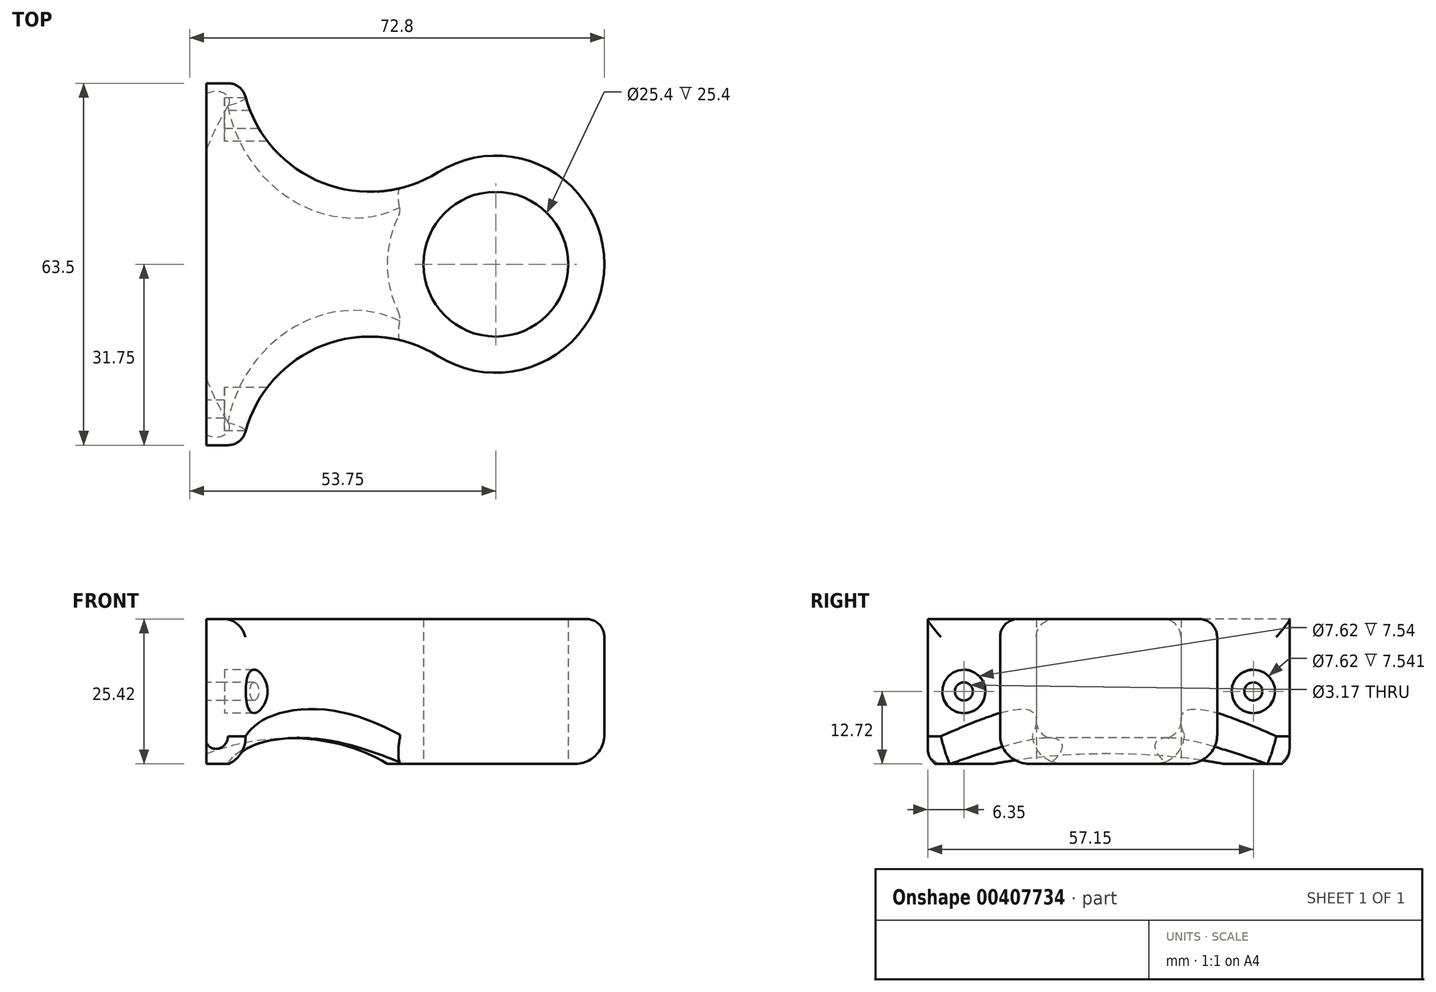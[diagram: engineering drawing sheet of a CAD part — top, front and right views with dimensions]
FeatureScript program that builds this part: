
annotation { "Feature Type Name" : "Feature", "Feature Type Description" : "" }
export const myFeature = defineFeature(function(context is Context, id is Id, definition is map)
    precondition{}
    {
        {
            var Q0;
            Q0=qCreatedBy(makeId("Top.planeOp"),FACE);
            var sketch = newSketch(context, id + "F0", { "sketchPlane" : qUnion([Q0])});
            skCircle(sketch, "E0", {"center": v(0, 0) * mm, "radius": 12.7 * mm});
            skCircle(sketch, "E1", {"center": v(0, 0) * mm, "radius": 19.05 * mm});
            skLineSegment(sketch, "E2", {"start": v(-44.45, 31.75) * mm, "end": v(-44.45, 0) * mm});
            skLineSegment(sketch, "E3", {"start": v(-50.8, 31.75) * mm, "end": v(-50.8, 0) * mm});
            skLineSegment(sketch, "E4", {"start": v(-50.8, 31.75) * mm, "end": v(-44.45, 31.75) * mm});
            skArc(sketch, "E5", {"start": v(-44.45, 31.75) * mm, "mid": v(-31.47, 14.73) * mm, "end": v(-10.1, 16.15) * mm});
            skArc(sketch, "E6.MirrorC", {"start": v(-44.45, -31.75) * mm, "mid": v(-31.47, -14.73) * mm, "end": v(-10.1, -16.15) * mm});
            skLineSegment(sketch, "E7.MirrorCS", {"start": v(-44.45, -31.75) * mm, "end": v(-44.45, 0) * mm});
            skLineSegment(sketch, "E8.MirrorCS", {"start": v(-50.8, -31.75) * mm, "end": v(-44.45, -31.75) * mm});
            skLineSegment(sketch, "E9.MirrorCS", {"start": v(-50.8, -31.75) * mm, "end": v(-50.8, 0) * mm});
            skSolve(sketch);
        }
        {
            var Q0;
            Q0=makeQuery(id+"F0.imprint","IMPRINT",FACE,{"disambiguationData":[TD([[makeQuery(id+"F0.imprint","IMPRINT",EDGE,{"derivedFrom":sQuery(id+"F0.wireOp",EDGE,"E2")}),1.0]])]});
            var Q1;
            Q1=makeQuery(id+"F0.imprint","IMPRINT",FACE,{"disambiguationData":[TD([[makeQuery(id+"F0.imprint","IMPRINT",EDGE,{"derivedFrom":sQuery(id+"F0.wireOp",EDGE,"E2")}),-1.0]])]});
            var Q2;
            Q2=makeQuery(id+"F0.imprint","IMPRINT",FACE,{"disambiguationData":[TD([[makeQuery(id+"F0.imprint","IMPRINT",EDGE,{"derivedFrom":sQuery(id+"F0.wireOp",EDGE,"E0")}),-1.0]])]});
            extrude(context, id + "F1", {"entities" : qUnion([Q0, Q1, Q2]), "depth" : 25.4 * mm, "offsetDistance" : 25.4 * mm});
        }
        {
            var Q0;
            Q0=makeQuery(id+"F1.opExtrude","CAP_VERTEX",VERTEX,{"disambiguationData":[OSD([sQuery(id+"F0.wireOp",EDGE,"E2"),sQuery(id+"F0.wireOp",EDGE,"E4"),sQuery(id+"F0.wireOp",EDGE,"E5")])],"isStart":true});
            var Q1;
            Q1=makeQuery(id+"F1.opExtrude","CAP_VERTEX",VERTEX,{"disambiguationData":[OSD([sQuery(id+"F0.wireOp",EDGE,"E1"),sQuery(id+"F0.wireOp",EDGE,"E5")])],"isStart":true});
            var Q2;
            Q2=makeQuery(id+"F1.opExtrude","CAP_VERTEX",VERTEX,{"disambiguationData":[OSD([sQuery(id+"F0.wireOp",EDGE,"E1"),sQuery(id+"F0.wireOp",EDGE,"E5")])],"isStart":false});
            cPlane(context, id + "F2", {"entities" : qUnion([Q0, Q1, Q2]), "cplaneType" : CPlaneType.THREE_POINT, "offset" : 25.4 * mm, "width" : 152.4 * mm, "height" : 152.4 * mm});
        }
        {
            var Q0;
            Q0=qCreatedBy(id+"F2.planeOp",FACE);
            var sketch = newSketch(context, id + "F3", { "sketchPlane" : qUnion([Q0])});
            skCircle(sketch, "E10", {"center": v(34.74, -37) * mm, "radius": 41.52 * mm});
            skLineSegment(sketch, "E11", {"start": v(8.8, 12.7) * mm, "end": v(68.21, 12.7) * mm});
            skCircle(sketch, "E12.MirrorC", {"center": v(34.74, 62.4) * mm, "radius": 41.52 * mm});
            skSolve(sketch);
        }
        {
            var Q0;
            Q0=makeQuery(id+"F3.imprint","IMPRINT",FACE,{"disambiguationData":[TD([[makeQuery(id+"F3.imprint","IMPRINT",EDGE,{"derivedFrom":sQuery(id+"F3.wireOp",EDGE,"E10")}),1.0]])]});
            var Q1;
            Q1=makeQuery(id+"F3.imprint","IMPRINT",FACE,{"disambiguationData":[TD([[makeQuery(id+"F3.imprint","IMPRINT",EDGE,{"derivedFrom":sQuery(id+"F3.wireOp",EDGE,"E12.MirrorC")}),-1.0]])]});
            var Q2;
            Q2=sQuery(id+"F0.wireOp",EDGE,"E1");
            sweep(context, id + "F4", {"operationType" : NewBodyOperationType.REMOVE, "profiles" : qUnion([Q0, Q1]), "path" : qUnion([Q2])});
        }
        {
            var Q0;
            Q0=makeQuery(id+"F1.opExtrude","SWEPT_FACE",FACE,{"disambiguationData":[OSD([sQuery(id+"F0.wireOp",EDGE,"E3"),sQuery(id+"F0.wireOp",EDGE,"E9.MirrorCS")])]});
            var sketch = newSketch(context, id + "F5", { "sketchPlane" : qUnion([Q0])});
            skCircle(sketch, "E13", {"center": v(25.4, 12.7) * mm, "radius": 3.81 * mm});
            skCircle(sketch, "E14", {"center": v(-25.4, 12.7) * mm, "radius": 3.81 * mm});
            skLineSegment(sketch, "E15", {"start": v(31.75, 12.7) * mm, "end": v(-31.75, 12.7) * mm});
            skCircle(sketch, "E16", {"center": v(25.4, 12.7) * mm, "radius": 1.59 * mm});
            skCircle(sketch, "E17", {"center": v(-25.4, 12.7) * mm, "radius": 1.59 * mm});
            skSolve(sketch);
        }
        {
            var Q0;
            {var subQ0=sQuery(id+"F5.wireOp",EDGE,"E16");var subQ1=sQuery(id+"F5.wireOp",EDGE,"E15");var subQ2=makeQuery(id+"F5.imprint","INTERSECT",VERTEX,{"disambiguationData":[OD(0.0)],"derivedFrom":[subQ1,subQ0]});Q0=makeQuery(id+"F5.imprint","IMPRINT",FACE,{"disambiguationData":[TD([[makeQuery(id+"F5.imprint","IMPRINT",EDGE,{"disambiguationData":[TD([[subQ2,-1.0]])],"derivedFrom":subQ1}),1.0]])]});}
            var Q1;
            {var subQ0=sQuery(id+"F5.wireOp",EDGE,"E16");var subQ1=sQuery(id+"F5.wireOp",EDGE,"E15");var subQ2=makeQuery(id+"F5.imprint","INTERSECT",VERTEX,{"disambiguationData":[OD(0.0)],"derivedFrom":[subQ1,subQ0]});Q1=makeQuery(id+"F5.imprint","IMPRINT",FACE,{"disambiguationData":[TD([[makeQuery(id+"F5.imprint","IMPRINT",EDGE,{"disambiguationData":[TD([[subQ2,-1.0]])],"derivedFrom":subQ1}),-1.0]])]});}
            var Q2;
            {var subQ0=sQuery(id+"F5.wireOp",EDGE,"E17");var subQ1=sQuery(id+"F5.wireOp",EDGE,"E15");var subQ2=makeQuery(id+"F5.imprint","INTERSECT",VERTEX,{"disambiguationData":[OD(0.0)],"derivedFrom":[subQ1,subQ0]});Q2=makeQuery(id+"F5.imprint","IMPRINT",FACE,{"disambiguationData":[TD([[makeQuery(id+"F5.imprint","IMPRINT",EDGE,{"disambiguationData":[TD([[subQ2,-1.0]])],"derivedFrom":subQ1}),-1.0]])]});}
            var Q3;
            {var subQ0=sQuery(id+"F5.wireOp",EDGE,"E17");var subQ1=sQuery(id+"F5.wireOp",EDGE,"E15");var subQ2=makeQuery(id+"F5.imprint","INTERSECT",VERTEX,{"disambiguationData":[OD(0.0)],"derivedFrom":[subQ1,subQ0]});Q3=makeQuery(id+"F5.imprint","IMPRINT",FACE,{"disambiguationData":[TD([[makeQuery(id+"F5.imprint","IMPRINT",EDGE,{"disambiguationData":[TD([[subQ2,-1.0]])],"derivedFrom":subQ1}),1.0]])]});}
            extrude(context, id + "F6", {"entities" : qUnion([Q0, Q1, Q2, Q3]), "operationType" : NewBodyOperationType.REMOVE, "oppositeDirection" : true, "depth" : 25.4 * mm, "offsetDistance" : 25.4 * mm});
        }
        {
            var Q0;
            {var subQ0=sQuery(id+"F5.wireOp",EDGE,"E15");var subQ1=sQuery(id+"F5.wireOp",EDGE,"E13");var subQ2=makeQuery(id+"F5.imprint","INTERSECT",VERTEX,{"disambiguationData":[OD(0.0)],"derivedFrom":[subQ1,subQ0]});Q0=makeQuery(id+"F5.imprint","IMPRINT",FACE,{"disambiguationData":[TD([[makeQuery(id+"F5.imprint","IMPRINT",EDGE,{"disambiguationData":[TD([[subQ2,1.0]])],"derivedFrom":subQ1}),1.0]])]});}
            var Q1;
            {var subQ0=sQuery(id+"F5.wireOp",EDGE,"E15");var subQ1=sQuery(id+"F5.wireOp",EDGE,"E13");var subQ2=makeQuery(id+"F5.imprint","INTERSECT",VERTEX,{"disambiguationData":[OD(0.0)],"derivedFrom":[subQ1,subQ0]});Q1=makeQuery(id+"F5.imprint","IMPRINT",FACE,{"disambiguationData":[TD([[makeQuery(id+"F5.imprint","IMPRINT",EDGE,{"disambiguationData":[TD([[subQ2,-1.0]])],"derivedFrom":subQ1}),1.0]])]});}
            var Q2;
            {var subQ0=sQuery(id+"F5.wireOp",EDGE,"E15");var subQ1=sQuery(id+"F5.wireOp",EDGE,"E14");var subQ2=makeQuery(id+"F5.imprint","INTERSECT",VERTEX,{"disambiguationData":[OD(0.0)],"derivedFrom":[subQ1,subQ0]});Q2=makeQuery(id+"F5.imprint","IMPRINT",FACE,{"disambiguationData":[TD([[makeQuery(id+"F5.imprint","IMPRINT",EDGE,{"disambiguationData":[TD([[subQ2,1.0]])],"derivedFrom":subQ1}),1.0]])]});}
            var Q3;
            {var subQ0=sQuery(id+"F5.wireOp",EDGE,"E15");var subQ1=sQuery(id+"F5.wireOp",EDGE,"E14");var subQ2=makeQuery(id+"F5.imprint","INTERSECT",VERTEX,{"disambiguationData":[OD(0.0)],"derivedFrom":[subQ1,subQ0]});Q3=makeQuery(id+"F5.imprint","IMPRINT",FACE,{"disambiguationData":[TD([[makeQuery(id+"F5.imprint","IMPRINT",EDGE,{"disambiguationData":[TD([[subQ2,-1.0]])],"derivedFrom":subQ1}),1.0]])]});}
            extrude(context, id + "F7", {"entities" : qUnion([Q0, Q1, Q2, Q3]), "operationType" : NewBodyOperationType.REMOVE, "oppositeDirection" : true, "depth" : 25.4 * mm, "offsetDistance" : 2.54 * mm, "offsetOppositeDirection" : true});
        }
        {
            var Q0;
            {var subQ0=sQuery(id+"F5.wireOp",EDGE,"E15");var subQ1=sQuery(id+"F5.wireOp",EDGE,"E14");var subQ2=makeQuery(id+"F5.imprint","INTERSECT",VERTEX,{"disambiguationData":[OD(0.0)],"derivedFrom":[subQ1,subQ0]});Q0=makeQuery(id+"F5.imprint","IMPRINT",FACE,{"disambiguationData":[TD([[makeQuery(id+"F5.imprint","IMPRINT",EDGE,{"disambiguationData":[TD([[subQ2,-1.0]])],"derivedFrom":subQ1}),1.0]])]});}
            var Q1;
            {var subQ0=sQuery(id+"F5.wireOp",EDGE,"E15");var subQ1=sQuery(id+"F5.wireOp",EDGE,"E14");var subQ2=makeQuery(id+"F5.imprint","INTERSECT",VERTEX,{"disambiguationData":[OD(0.0)],"derivedFrom":[subQ1,subQ0]});Q1=makeQuery(id+"F5.imprint","IMPRINT",FACE,{"disambiguationData":[TD([[makeQuery(id+"F5.imprint","IMPRINT",EDGE,{"disambiguationData":[TD([[subQ2,1.0]])],"derivedFrom":subQ1}),1.0]])]});}
            var Q2;
            {var subQ0=sQuery(id+"F5.wireOp",EDGE,"E15");var subQ1=sQuery(id+"F5.wireOp",EDGE,"E13");var subQ2=makeQuery(id+"F5.imprint","INTERSECT",VERTEX,{"disambiguationData":[OD(0.0)],"derivedFrom":[subQ1,subQ0]});Q2=makeQuery(id+"F5.imprint","IMPRINT",FACE,{"disambiguationData":[TD([[makeQuery(id+"F5.imprint","IMPRINT",EDGE,{"disambiguationData":[TD([[subQ2,1.0]])],"derivedFrom":subQ1}),1.0]])]});}
            var Q3;
            {var subQ0=sQuery(id+"F5.wireOp",EDGE,"E15");var subQ1=sQuery(id+"F5.wireOp",EDGE,"E13");var subQ2=makeQuery(id+"F5.imprint","INTERSECT",VERTEX,{"disambiguationData":[OD(0.0)],"derivedFrom":[subQ1,subQ0]});Q3=makeQuery(id+"F5.imprint","IMPRINT",FACE,{"disambiguationData":[TD([[makeQuery(id+"F5.imprint","IMPRINT",EDGE,{"disambiguationData":[TD([[subQ2,-1.0]])],"derivedFrom":subQ1}),1.0]])]});}
            extrude(context, id + "F8", {"entities" : qUnion([Q0, Q1, Q2, Q3]), "operationType" : NewBodyOperationType.ADD, "oppositeDirection" : true, "depth" : 3.17 * mm, "offsetDistance" : 25.4 * mm});
        }
        {
            var Q0;
            Q0=makeQuery(id+"F4.boolean.opBoolean","INTERSECT",EDGE,{"derivedFrom":[makeQuery(id+"F1.opExtrude","SWEPT_FACE",FACE,{"disambiguationData":[OSD([sQuery(id+"F0.wireOp",EDGE,"E5")])]}),makeQuery(id+"F4.opSweep","SWEPT_FACE",FACE,{"disambiguationData":[OSD([sQuery(id+"F0.wireOp",EDGE,"E1"),sQuery(id+"F3.wireOp",EDGE,"E10")])]})]});
            var Q1;
            Q1=makeQuery(id+"F4.boolean.opBoolean","INTERSECT",EDGE,{"derivedFrom":[makeQuery(id+"F1.opExtrude","SWEPT_FACE",FACE,{"disambiguationData":[OSD([sQuery(id+"F0.wireOp",EDGE,"E5")])]}),makeQuery(id+"F4.opSweep","SWEPT_FACE",FACE,{"disambiguationData":[OSD([sQuery(id+"F0.wireOp",EDGE,"E1"),sQuery(id+"F3.wireOp",EDGE,"E12.MirrorC")])]})]});
            var Q2;
            Q2=makeQuery(id+"F4.boolean.opBoolean","INTERSECT",EDGE,{"derivedFrom":[makeQuery(id+"F1.opExtrude","SWEPT_FACE",FACE,{"disambiguationData":[OSD([sQuery(id+"F0.wireOp",EDGE,"E6.MirrorC")])]}),makeQuery(id+"F4.opSweep","SWEPT_FACE",FACE,{"disambiguationData":[OSD([sQuery(id+"F0.wireOp",EDGE,"E1"),sQuery(id+"F3.wireOp",EDGE,"E12.MirrorC")])]})]});
            var Q3;
            Q3=makeQuery(id+"F4.boolean.opBoolean","INTERSECT",EDGE,{"derivedFrom":[makeQuery(id+"F1.opExtrude","SWEPT_FACE",FACE,{"disambiguationData":[OSD([sQuery(id+"F0.wireOp",EDGE,"E6.MirrorC")])]}),makeQuery(id+"F4.opSweep","SWEPT_FACE",FACE,{"disambiguationData":[OSD([sQuery(id+"F0.wireOp",EDGE,"E1"),sQuery(id+"F3.wireOp",EDGE,"E10")])]})]});
            fillet(context, id + "F9", {"entities" : qUnion([Q0, Q1, Q2, Q3]), "radius" : 5.08 * mm, "tangentPropagation" : true, "allowEdgeOverflow" : false});
        }
        {
            var Q0;
            Q0=makeQuery(id+"F1.opExtrude","CAP_EDGE",EDGE,{"disambiguationData":[OSD([sQuery(id+"F0.wireOp",EDGE,"E1")])],"isStart":true});
            var Q1;
            Q1=makeQuery(id+"F1.opExtrude","CAP_EDGE",EDGE,{"disambiguationData":[OSD([sQuery(id+"F0.wireOp",EDGE,"E1")])],"isStart":false});
            var Q2;
            Q2=makeQuery(id+"F1.opExtrude","SWEPT_EDGE",EDGE,{"disambiguationData":[OSD([sQuery(id+"F0.wireOp",EDGE,"E2"),sQuery(id+"F0.wireOp",EDGE,"E4"),sQuery(id+"F0.wireOp",EDGE,"E5")])]});
            var Q3;
            Q3=makeQuery(id+"F1.opExtrude","SWEPT_EDGE",EDGE,{"disambiguationData":[OSD([sQuery(id+"F0.wireOp",EDGE,"E6.MirrorC"),sQuery(id+"F0.wireOp",EDGE,"E7.MirrorCS"),sQuery(id+"F0.wireOp",EDGE,"E8.MirrorCS")])]});
            fillet(context, id + "F10", {"entities" : qUnion([Q0, Q1, Q2, Q3]), "radius" : 3.17 * mm, "tangentPropagation" : true, "allowEdgeOverflow" : false});
        }
    });
